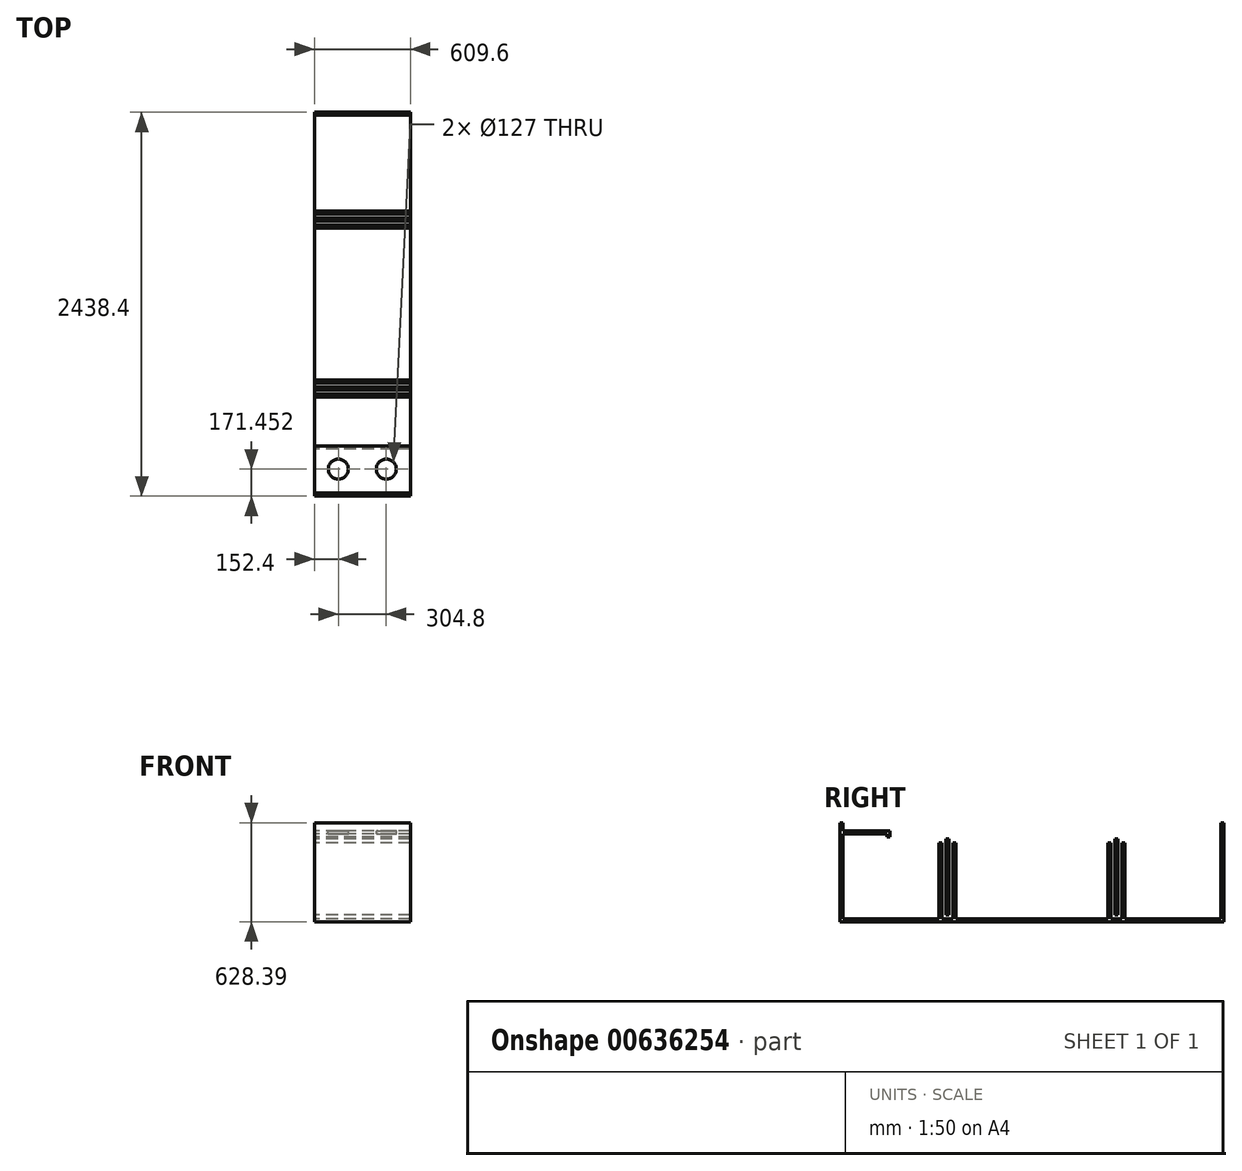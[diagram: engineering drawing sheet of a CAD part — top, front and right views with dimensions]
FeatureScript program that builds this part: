
annotation { "Feature Type Name" : "Feature", "Feature Type Description" : "" }
export const myFeature = defineFeature(function(context is Context, id is Id, definition is map)
    precondition{}
    {
        {
            var Q0;
            Q0=qCreatedBy(makeId("Right.planeOp"),FACE);
            var sketch = newSketch(context, id + "F0", { "sketchPlane" : qUnion([Q0])});
            skLineSegment(sketch, "E0.bottom", {"start": v(-65.76, 601.44) * mm, "end": v(2372.64, 601.44) * mm});
            skLineSegment(sketch, "E0.top", {"start": v(-46.7, -8.16) * mm, "end": v(562.9, -8.16) * mm});
            skLineSegment(sketch, "E0.left", {"start": v(-65.76, 601.44) * mm, "end": v(-65.76, -8.16) * mm});
            skLineSegment(sketch, "E0.right", {"start": v(2372.64, 601.44) * mm, "end": v(2372.64, -8.16) * mm});
            skLineSegment(sketch, "E1", {"start": v(-46.7, 601.44) * mm, "end": v(-46.7, 550.64) * mm});
            skLineSegment(sketch, "E2", {"start": v(-46.7, 550.64) * mm, "end": v(251.5, 550.64) * mm});
            skLineSegment(sketch, "E3", {"start": v(232.46, 531.6) * mm, "end": v(-46.7, 531.6) * mm});
            skLineSegment(sketch, "E4", {"start": v(-46.7, 531.6) * mm, "end": v(232.46, 531.6) * mm});
            skLineSegment(sketch, "E5", {"start": v(251.5, 512.54) * mm, "end": v(232.46, 512.54) * mm});
            skLineSegment(sketch, "E6", {"start": v(232.46, 512.54) * mm, "end": v(232.46, 531.6) * mm});
            skLineSegment(sketch, "E7.trimOffspring", {"start": v(-46.7, 531.6) * mm, "end": v(-46.7, -8.16) * mm});
            skPoint(sketch, "E8.end.orphan", {"position": v(251.5, 531.6) * mm});
            skLineSegment(sketch, "E9", {"start": v(251.5, 550.64) * mm, "end": v(251.5, 512.54) * mm});
            skLineSegment(sketch, "E10", {"start": v(-65.76, -8.16) * mm, "end": v(-65.76, -26.95) * mm});
            skLineSegment(sketch, "E11", {"start": v(-65.76, -26.95) * mm, "end": v(2372.64, -26.95) * mm});
            skLineSegment(sketch, "E12", {"start": v(2372.64, -26.95) * mm, "end": v(2372.64, -8.16) * mm});
            skLineSegment(sketch, "E13", {"start": v(562.9, 474.44) * mm, "end": v(562.9, -8.16) * mm});
            skLineSegment(sketch, "E14", {"start": v(581.94, -8.16) * mm, "end": v(581.94, 474.44) * mm});
            skLineSegment(sketch, "E15", {"start": v(581.94, 474.44) * mm, "end": v(562.9, 474.44) * mm});
            skLineSegment(sketch, "E16", {"start": v(607.34, 17.24) * mm, "end": v(607.34, 499.84) * mm});
            skLineSegment(sketch, "E17", {"start": v(607.34, 499.84) * mm, "end": v(626.4, 499.84) * mm});
            skLineSegment(sketch, "E18", {"start": v(626.4, 499.84) * mm, "end": v(626.4, 17.24) * mm});
            skLineSegment(sketch, "E19", {"start": v(626.4, 17.24) * mm, "end": v(607.34, 17.24) * mm});
            skLineSegment(sketch, "E20", {"start": v(651.8, -8.16) * mm, "end": v(651.8, 474.44) * mm});
            skLineSegment(sketch, "E21", {"start": v(651.8, 474.44) * mm, "end": v(670.84, 474.44) * mm});
            skLineSegment(sketch, "E22", {"start": v(670.84, 474.44) * mm, "end": v(670.84, -8.16) * mm});
            skLineSegment(sketch, "E23", {"start": v(1636.04, -8.16) * mm, "end": v(1636.04, 474.44) * mm});
            skLineSegment(sketch, "E24", {"start": v(1636.04, 474.44) * mm, "end": v(1655.1, 474.44) * mm});
            skLineSegment(sketch, "E25", {"start": v(1655.1, 474.44) * mm, "end": v(1655.1, -8.16) * mm});
            skLineSegment(sketch, "E26", {"start": v(1680.5, 499.84) * mm, "end": v(1699.54, 499.84) * mm});
            skLineSegment(sketch, "E27", {"start": v(1699.54, 499.84) * mm, "end": v(1699.54, 17.24) * mm});
            skLineSegment(sketch, "E28", {"start": v(1699.54, 17.24) * mm, "end": v(1680.5, 17.24) * mm});
            skLineSegment(sketch, "E29", {"start": v(1680.5, 17.24) * mm, "end": v(1680.5, 499.84) * mm});
            skLineSegment(sketch, "E30", {"start": v(1724.94, -8.16) * mm, "end": v(1724.94, 474.44) * mm});
            skLineSegment(sketch, "E31", {"start": v(1724.94, 474.44) * mm, "end": v(1744, 474.44) * mm});
            skLineSegment(sketch, "E32", {"start": v(1744, 474.44) * mm, "end": v(1744, -8.16) * mm});
            skLineSegment(sketch, "E33", {"start": v(2353.6, -8.16) * mm, "end": v(2353.6, 601.44) * mm});
            skLineSegment(sketch, "E34.trimOffspring", {"start": v(1744, -8.16) * mm, "end": v(2353.6, -8.16) * mm});
            skLineSegment(sketch, "E35.trimOffspring", {"start": v(1655.1, -8.16) * mm, "end": v(1724.94, -8.16) * mm});
            skLineSegment(sketch, "E36.trimOffspring", {"start": v(670.84, -8.16) * mm, "end": v(1636.04, -8.16) * mm});
            skLineSegment(sketch, "E37.trimOffspring", {"start": v(581.94, -8.16) * mm, "end": v(651.8, -8.16) * mm});
            skSolve(sketch);
        }
        {
            var Q0;
            Q0=makeQuery(id+"F0.imprint","IMPRINT",FACE,{"disambiguationData":[TD([[makeQuery(id+"F0.imprint","IMPRINT",EDGE,{"derivedFrom":sQuery(id+"F0.wireOp",EDGE,"E0.top")}),-1.0]])]});
            var Q1;
            Q1=makeQuery(id+"F0.imprint","IMPRINT",FACE,{"disambiguationData":[TD([[makeQuery(id+"F0.imprint","IMPRINT",EDGE,{"derivedFrom":sQuery(id+"F0.wireOp",EDGE,"E16")}),-1.0]])]});
            var Q2;
            Q2=makeQuery(id+"F0.imprint","IMPRINT",FACE,{"disambiguationData":[TD([[makeQuery(id+"F0.imprint","IMPRINT",EDGE,{"derivedFrom":sQuery(id+"F0.wireOp",EDGE,"E26")}),-1.0]])]});
            extrude(context, id + "F1", {"entities" : qUnion([Q0, Q1, Q2]), "depth" : 609.6 * mm, "offsetDistance" : 25.4 * mm});
        }
        {
            var Q0;
            Q0=makeQuery(id+"F1.opExtrude","SWEPT_FACE",FACE,{"disambiguationData":[OSD([sQuery(id+"F0.wireOp",EDGE,"E2")])]});
            var sketch = newSketch(context, id + "F2", { "sketchPlane" : qUnion([Q0])});
            skCircle(sketch, "E38", {"center": v(152.4, 105.7) * mm, "radius": 63.5 * mm});
            skCircle(sketch, "E39", {"center": v(457.2, 105.7) * mm, "radius": 63.5 * mm});
            skSolve(sketch);
        }
        {
            var Q0;
            Q0=sQuery(id+"F2.wireOp",VERTEX,"E38.center");
            var Q1;
            Q1=sQuery(id+"F2.wireOp",VERTEX,"E39.center");
            var Q2;
            Q2=makeQuery(id+"F1.opExtrude","SWEPT_BODY",BODY,{"disambiguationData":[OSD([sQuery(id+"F0.wireOp",EDGE,"E0.bottom"),sQuery(id+"F0.wireOp",EDGE,"E0.top"),sQuery(id+"F0.wireOp",EDGE,"E0.left"),sQuery(id+"F0.wireOp",EDGE,"E0.right"),sQuery(id+"F0.wireOp",EDGE,"E1"),sQuery(id+"F0.wireOp",EDGE,"E2"),sQuery(id+"F0.wireOp",EDGE,"E4"),sQuery(id+"F0.wireOp",EDGE,"E5"),sQuery(id+"F0.wireOp",EDGE,"E6"),sQuery(id+"F0.wireOp",EDGE,"E7.trimOffspring"),sQuery(id+"F0.wireOp",EDGE,"E9"),sQuery(id+"F0.wireOp",EDGE,"E10"),sQuery(id+"F0.wireOp",EDGE,"E11"),sQuery(id+"F0.wireOp",EDGE,"E12"),sQuery(id+"F0.wireOp",EDGE,"E13"),sQuery(id+"F0.wireOp",EDGE,"E14"),sQuery(id+"F0.wireOp",EDGE,"E15"),sQuery(id+"F0.wireOp",EDGE,"E20"),sQuery(id+"F0.wireOp",EDGE,"E21"),sQuery(id+"F0.wireOp",EDGE,"E22"),sQuery(id+"F0.wireOp",EDGE,"E23"),sQuery(id+"F0.wireOp",EDGE,"E24"),sQuery(id+"F0.wireOp",EDGE,"E25"),sQuery(id+"F0.wireOp",EDGE,"E30"),sQuery(id+"F0.wireOp",EDGE,"E31"),sQuery(id+"F0.wireOp",EDGE,"E32"),sQuery(id+"F0.wireOp",EDGE,"E33"),sQuery(id+"F0.wireOp",EDGE,"E34.trimOffspring"),sQuery(id+"F0.wireOp",EDGE,"E35.trimOffspring"),sQuery(id+"F0.wireOp",EDGE,"E36.trimOffspring"),sQuery(id+"F0.wireOp",EDGE,"E37.trimOffspring")])]});
            hole(context, id + "F3", {"style" : HoleStyle.SIMPLE, "endStyle" : HoleEndStyle.BLIND, "holeDiameter" : 127 * mm, "majorDiameter" : 6.35 * mm, "holeDepth" : 19.05 * mm, "isTappedThrough" : true, "tappedDepth" : 12.7 * mm, "tapClearance" : 3, "locations" : qUnion([Q0, Q1]), "scope" : qUnion([Q2])});
        }
    });
